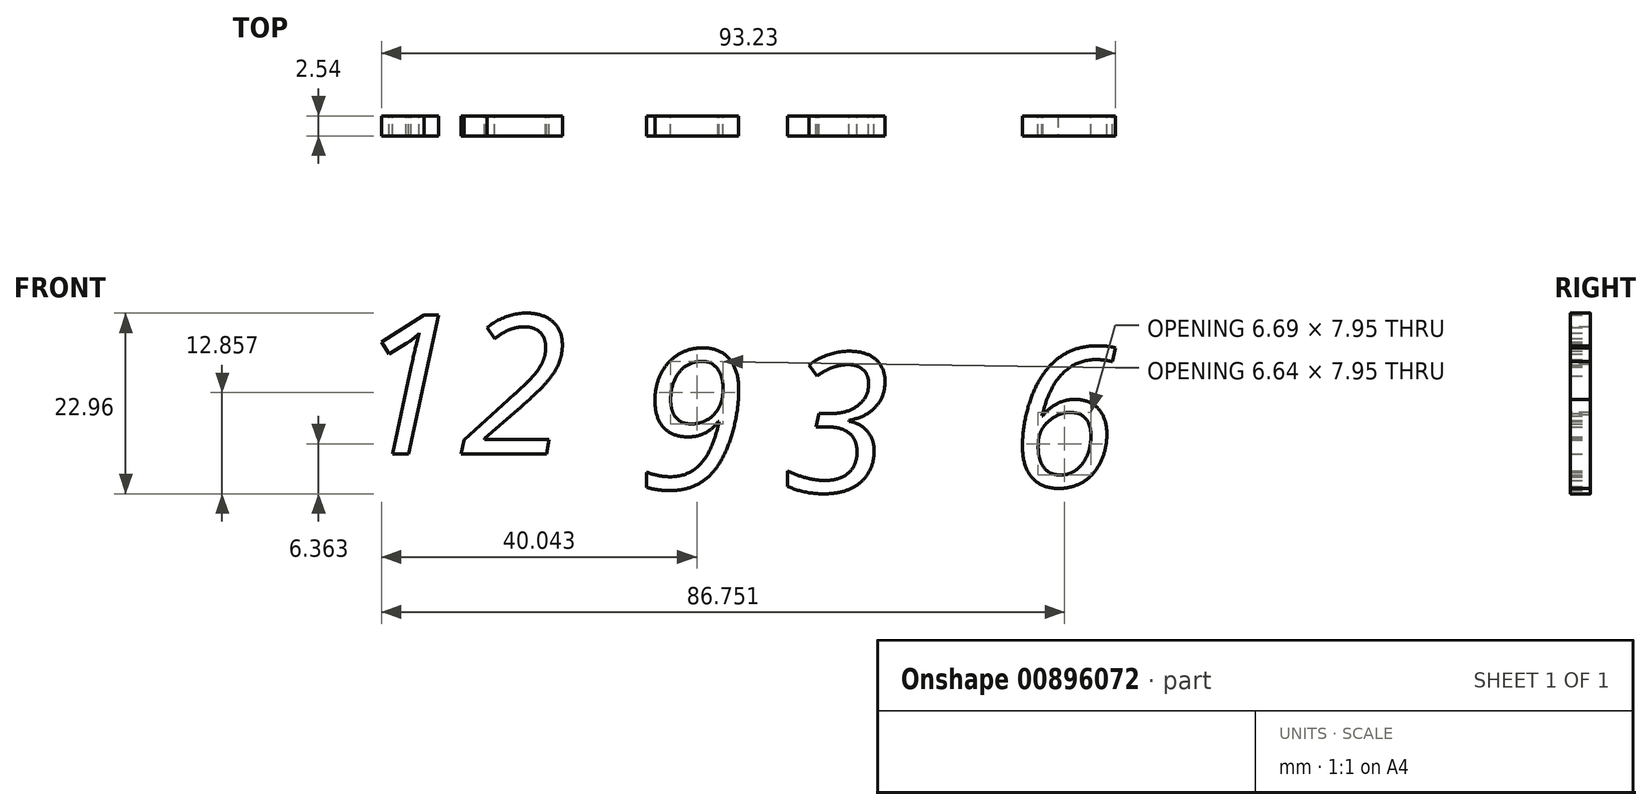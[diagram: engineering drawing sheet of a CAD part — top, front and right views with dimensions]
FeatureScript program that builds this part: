
annotation { "Feature Type Name" : "Feature", "Feature Type Description" : "" }
export const myFeature = defineFeature(function(context is Context, id is Id, definition is map)
    precondition{}
    {
        {
            var Q0;
            Q0=qCreatedBy(makeId("Front.planeOp"),FACE);
            var sketch = newSketch(context, id + "F0", { "sketchPlane" : qUnion([Q0])});
            skText(sketch, "E0", { "text": "3", "fontName": "OpenSans-Italic.ttf"});
            skText(sketch, "E1", { "text": "12", "fontName": "OpenSans-Italic.ttf"});
            skText(sketch, "E2", { "text": "6", "fontName": "OpenSans-Italic.ttf"});
            skText(sketch, "E3", { "text": "9", "fontName": "OpenSans-Italic.ttf"});
            const initialGuessF0  = {"E0": [0.00226, 0.02774, 1, 0, 0.01778], "E1": [-0.0524, 0.03258, 1, 0, 0.01778], "E2": [0.03105, 0.02843, 1, 0, 0.01778], "E3": [-0.01625, 0.02816, 1, 0, 0.01778]};
            skSetInitialGuess(sketch, initialGuessF0);
            skSolve(sketch);
        }
        {
            var Q0;
            Q0 = qSketchRegion(id + "F0", true);
            extrude(context, id + "F1", {"entities" : qUnion([Q0]), "depth" : 2.54 * mm, "offsetDistance" : 25.4 * mm});
        }
    });
